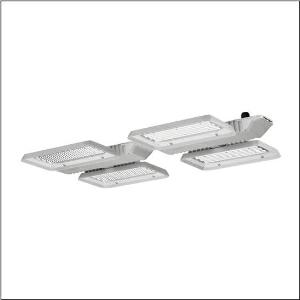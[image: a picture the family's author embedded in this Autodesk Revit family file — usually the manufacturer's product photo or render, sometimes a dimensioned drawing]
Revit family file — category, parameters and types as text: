
# Revit family: highbay_11_51hla2d24nca
name_source: partatom
category: Lighting Fixtures
units: mm (PartAtom-declared; Revit-internal decimal feet)

## family parameters
Cut with Voids When Loaded = No
Host = Face
Light Source = No
Part Type = Normal
Room Calculation Point = No
Round Connector Dimension = Use Diameter
Shared = No

## types (1)
- --- (1 x LED, 33150 lm, 189.6 W, 4000K)
    Apparent Load = 190 VA
    CIE Flux Codes = 89 96 99 100 100
    Color Rendering = 80
    Color Temperature = 4000K
    Default Elevation = 1800 mm
    Description = Highbay 11, LED high bay luminaire, primary light control with lens, of PMMA, light emission: direct distribution, primary light characteristic: symmetric, installation type: surface-mounted, suspended mounting, for 2x 2x LED, rated luminous flux: 33.150lm, luminous efficacy: 175lm/W, light colour: 840, colour temperature: 4000K, control gear: ECG DALI, with terminal, 5-pole, max. 2.5mm², mains connection: 230..240V, AC, 50/60Hz, rated input power: 190W, LED unit, of diecast aluminium, unplated, bead blasted, silver, length: 940mm, width: 500mm, height: 65mm, housing, of diecast aluminium, uncoated, bead blasted, silver, protection rating (complete): IP65, insulation class (complete): insulation class I (protective earthing), certification: CE, ENEC, VDE, UKCA, protection symbol: D, impact resistance: IK08 with glass or PC cover, permissible operating ambient temperature: -35..+45°C, reducing of maximum allowable ambient temperature of 5°C with ceiling mounting, corresponds to IFS (International Featured Standards) requirements for safety and quality in the food industry, packaging unit: 1 piece
    Height = 95 mm
    Lamp = 1 x LED
    Lamp Light Flux = 33150 lm
    Lamp Power = 189.6 W
    Lamp count = 1
    Length = 939 mm
    Luminous efficacy = 175 lm/W
    Manufacturer = Siteco
    ModVariant = No
    Model = 51HLA2D24NCA
    Mounting Place = Ceiling
    Mounting Type = Pendant
    Number of Poles = 1
    OnlyDefault = Yes
    Power Factor = 1
    Product Name = Highbay 11
    Product group = LED high bay luminaire
    ProductGroupID = 903
    Protection Class = Protection class I
    Protection Degree = IP 65
    RLX_Detail_Level = 1
    RLX_Emergency_Light_Flux = 0 lm
    RLX_Emergency_Type = 0
    RLX_Emergency_Type_DB = No
    RlxData = <blob elided: 96853 chars, md5=16c9584b>
    Socket = socket
    Standby Power = 0 W
    System Light Flux = 33150 lm
    System Power = 190 W
    Type Comments = factory setting: luminous flux: 100 % | dim-lin: 254 | 535 mA
    Type Image = l_1003428.jpg
    URL = http://relux.com
    VarID = @adj_177363
    Voltage = 0 V
    Weight = 0.00 kg
    Width = 501 mm

## geometry (parser evidence)
native form markers: Blend x4, Sweep x10
no freeform markers — native parametric forms only
